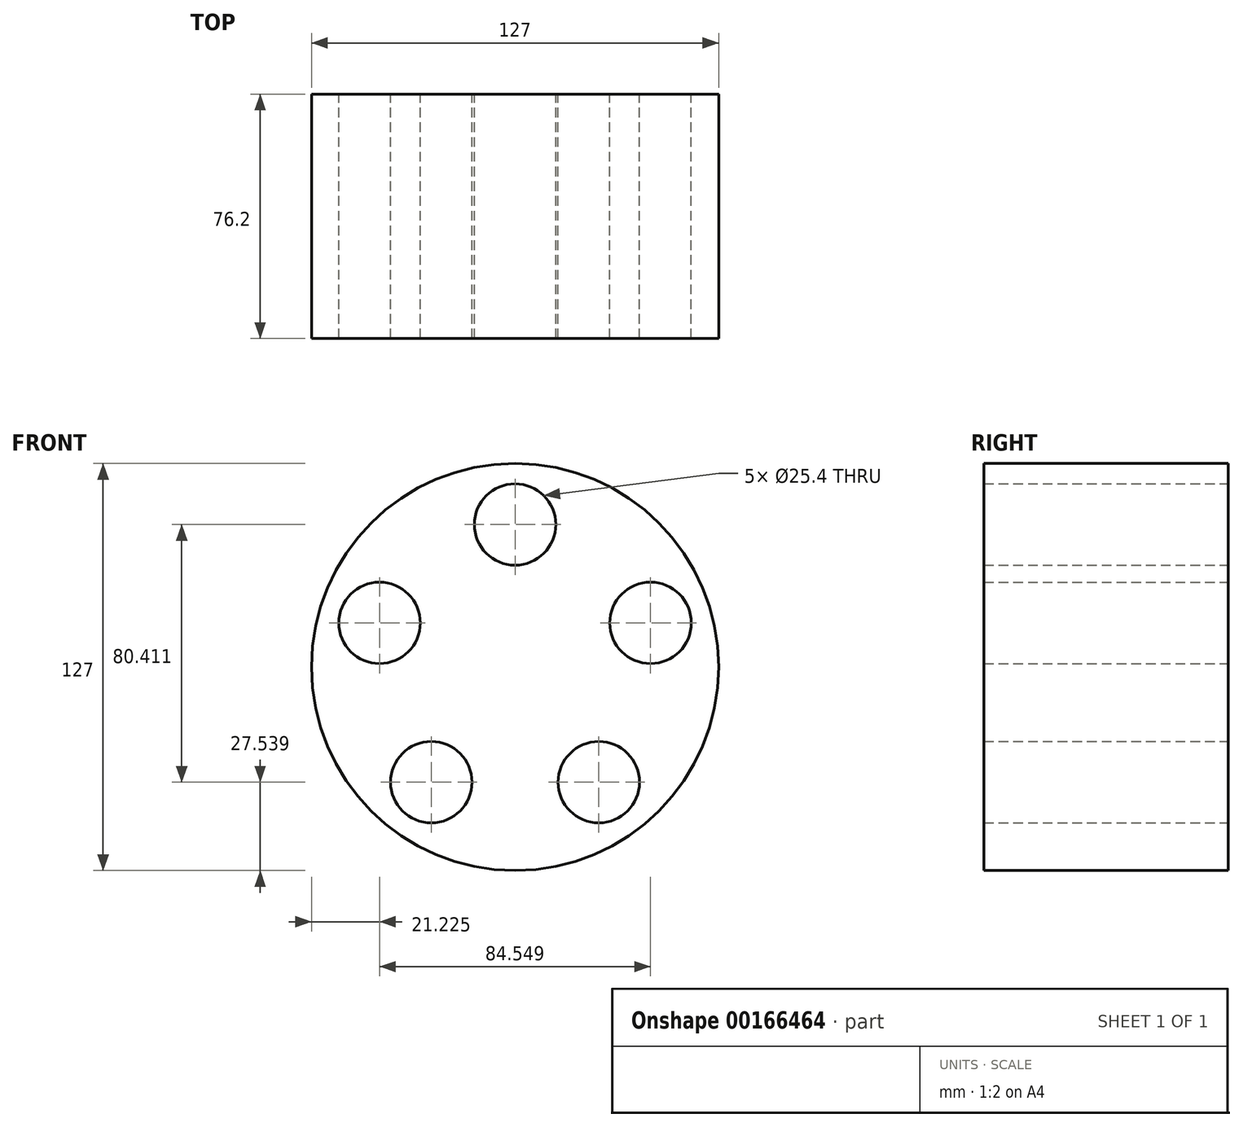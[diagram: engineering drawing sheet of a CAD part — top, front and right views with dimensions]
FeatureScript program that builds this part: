
annotation { "Feature Type Name" : "Feature", "Feature Type Description" : "" }
export const myFeature = defineFeature(function(context is Context, id is Id, definition is map)
    precondition{}
    {
        {
            var Q0;
            Q0=qCreatedBy(makeId("Front.planeOp"),FACE);
            var sketch = newSketch(context, id + "F0", { "sketchPlane" : qUnion([Q0])});
            skCircle(sketch, "E0", {"center": v(0, 0) * mm, "radius": 63.5 * mm});
            skCircle(sketch, "E1", {"center": v(0, 44.45) * mm, "radius": 12.7 * mm});
            skCircle(sketch, "E2.1.0", {"center": v(-42.27, 13.74) * mm, "radius": 12.7 * mm});
            skCircle(sketch, "E2.2.0", {"center": v(-26.13, -35.96) * mm, "radius": 12.7 * mm});
            skCircle(sketch, "E2.3.0", {"center": v(26.13, -35.96) * mm, "radius": 12.7 * mm});
            skCircle(sketch, "E2.4.0", {"center": v(42.27, 13.74) * mm, "radius": 12.7 * mm});
            skSolve(sketch);
        }
        {
            var Q0;
            Q0=makeQuery(id+"F0.imprint","IMPRINT",FACE,{"disambiguationData":[TD([[makeQuery(id+"F0.imprint","IMPRINT",EDGE,{"derivedFrom":sQuery(id+"F0.wireOp",EDGE,"E0")}),1.0]])]});
            extrude(context, id + "F1", {"entities" : qUnion([Q0]), "depth" : 76.2 * mm});
        }
    });
